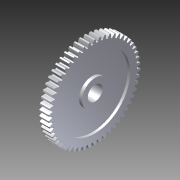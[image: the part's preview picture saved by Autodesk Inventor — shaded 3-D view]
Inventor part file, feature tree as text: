
AUTODESK INVENTOR PART (.ipt)
format: ipt  version: 2012 (Build 160160000, 160)  size: 1,035,264 bytes
history: native  units: in
note: dims shown in document units (in); Inventor stores cm internally (conversion verified against a paired STEP export)
features: extrude x2, sketch x1, imported_body x1
ambient origin geometry x8: Origin, YZ Plane, XZ Plane, XY Plane, X Axis, Y Axis, Z Axis, Center Point
feature tree (4):
  sketch  "Sketch1"  dims[d0=0.375in d3=0.3in d4=0.0in d5=1.0in d6=0.125in d7=0.125in d8=0.0625in d9=0.5625in d10=0.3in d11=0.0in]
  extrude  "Extrusion2"  Depth=0.3in TaperAngle=0.0deg
  extrude  "Extrusion3"  Depth=1.0in
  imported_body  "Base1"
